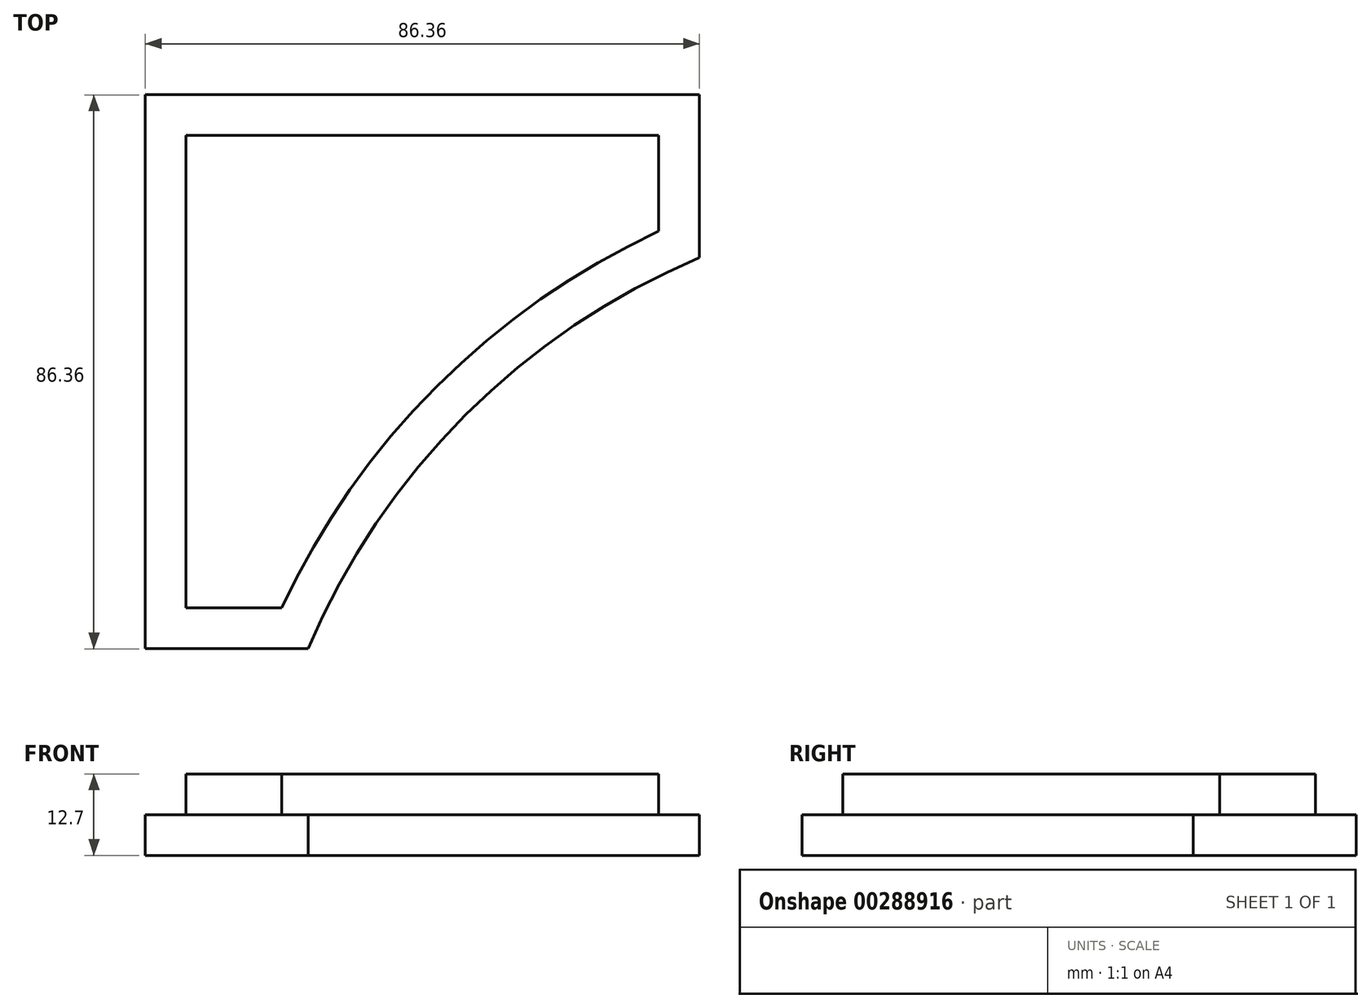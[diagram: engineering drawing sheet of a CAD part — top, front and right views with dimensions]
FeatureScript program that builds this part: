
annotation { "Feature Type Name" : "Feature", "Feature Type Description" : "" }
export const myFeature = defineFeature(function(context is Context, id is Id, definition is map)
    precondition{}
    {
        {
            var Q0;
            Q0=qCreatedBy(makeId("Top.planeOp"),FACE);
            var sketch = newSketch(context, id + "F0", { "sketchPlane" : qUnion([Q0])});
            skLineSegment(sketch, "E0.bottom", {"start": v(-130.73, 130.73) * mm, "end": v(-44.37, 130.73) * mm});
            skLineSegment(sketch, "E0.left", {"start": v(-130.73, 130.73) * mm, "end": v(-130.73, 44.37) * mm});
            skPoint(sketch, "E0.middle", {"position": v(0, 0) * mm});
            skArc(sketch, "E1", {"start": v(-44.37, 105.33) * mm, "mid": v(-80.82, 80.82) * mm, "end": v(-105.33, 44.37) * mm});
            skLineSegment(sketch, "E2.bottom", {"start": v(-130.73, 44.37) * mm, "end": v(-105.33, 44.37) * mm});
            skLineSegment(sketch, "E3.left", {"start": v(-44.37, 130.73) * mm, "end": v(-44.37, 105.33) * mm});
            skSolve(sketch);
        }
        {
            var Q0;
            Q0 = qSketchRegion(id + "F0", true);
            extrude(context, id + "F1", {"entities" : qUnion([Q0]), "depth" : 12.7 * mm});
        }
        {
            var Q0;
            Q0=makeQuery(id+"F1.opExtrude","CAP_FACE",FACE,{"disambiguationData":[OSD([sQuery(id+"F0.wireOp",EDGE,"E0.bottom"),sQuery(id+"F0.wireOp",EDGE,"E0.left"),sQuery(id+"F0.wireOp",EDGE,"E1"),sQuery(id+"F0.wireOp",EDGE,"E2.bottom"),sQuery(id+"F0.wireOp",EDGE,"E3.left")])],"isStart":false});
            var sketch = newSketch(context, id + "F2", { "sketchPlane" : qUnion([Q0])});
            skLineSegment(sketch, "E4", {"start": v(-130.73, 130.73) * mm, "end": v(-44.37, 130.73) * mm});
            skLineSegment(sketch, "E5", {"start": v(-44.37, 130.73) * mm, "end": v(-44.37, 105.33) * mm});
            skLineSegment(sketch, "E6", {"start": v(-130.73, 130.73) * mm, "end": v(-130.73, 44.37) * mm});
            skLineSegment(sketch, "E7", {"start": v(-130.73, 44.37) * mm, "end": v(-105.33, 44.37) * mm});
            skArc(sketch, "E8", {"start": v(-44.37, 105.33) * mm, "mid": v(-80.8, 80.8) * mm, "end": v(-105.33, 44.37) * mm});
            skLineSegment(sketch, "E9.0", {"start": v(-50.72, 124.38) * mm, "end": v(-50.72, 109.47) * mm});
            skLineSegment(sketch, "E9.1", {"start": v(-124.38, 124.38) * mm, "end": v(-50.72, 124.38) * mm});
            skArc(sketch, "E9.2", {"start": v(-50.72, 109.47) * mm, "mid": v(-85.3, 85.3) * mm, "end": v(-109.47, 50.72) * mm});
            skLineSegment(sketch, "E9.3", {"start": v(-124.38, 50.72) * mm, "end": v(-109.47, 50.72) * mm});
            skLineSegment(sketch, "E9.4", {"start": v(-124.38, 124.38) * mm, "end": v(-124.38, 50.72) * mm});
            skSolve(sketch);
        }
        {
            var Q0;
            Q0=makeQuery(id+"F2.imprint","IMPRINT",FACE,{"disambiguationData":[TD([[makeQuery(id+"F2.imprint","IMPRINT",EDGE,{"derivedFrom":sQuery(id+"F2.wireOp",EDGE,"E4")}),-1.0]])]});
            var Q1;
            Q1 = qConstructionFilter(qBodyType(qCreatedBy(id + "F2" ,EDGE), BodyType.WIRE), ConstructionObject.NO);
            extrude(context, id + "F3", {"entities" : qUnion([Q0]), "operationType" : NewBodyOperationType.REMOVE, "surfaceEntities" : qUnion([Q1]), "oppositeDirection" : true, "depth" : 6.35 * mm});
        }
    });
